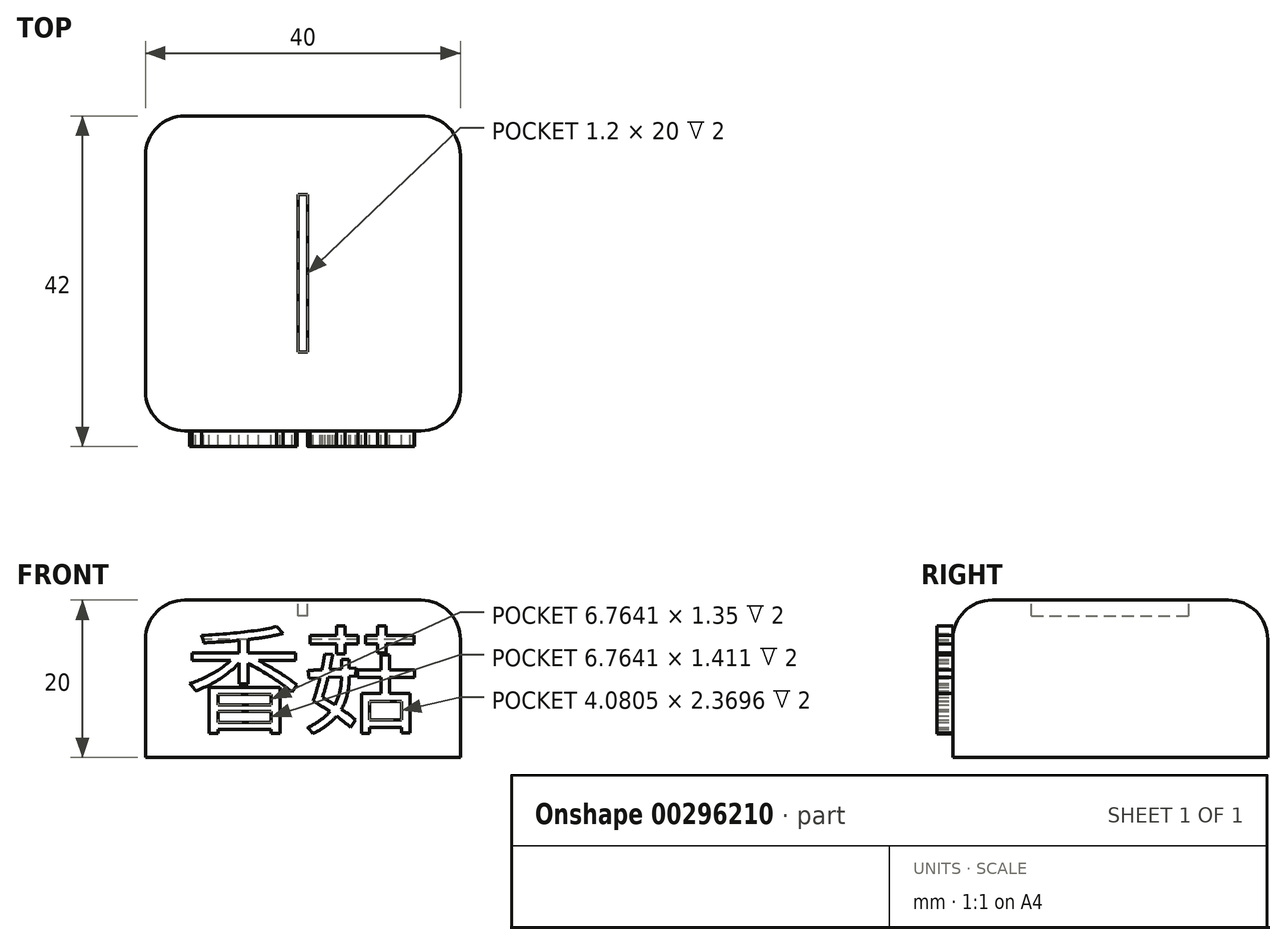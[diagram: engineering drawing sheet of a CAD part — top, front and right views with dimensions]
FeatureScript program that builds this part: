
annotation { "Feature Type Name" : "Feature", "Feature Type Description" : "" }
export const myFeature = defineFeature(function(context is Context, id is Id, definition is map)
    precondition{}
    {
        {
            var Q0;
            Q0=qCreatedBy(makeId("Top.planeOp"),FACE);
            var sketch = newSketch(context, id + "F0", { "sketchPlane" : qUnion([Q0])});
            skLineSegment(sketch, "E0.bottom", {"start": v(20, -20) * mm, "end": v(-20, -20) * mm});
            skLineSegment(sketch, "E0.top", {"start": v(20, 20) * mm, "end": v(-20, 20) * mm});
            skLineSegment(sketch, "E0.left", {"start": v(20, -20) * mm, "end": v(20, 20) * mm});
            skLineSegment(sketch, "E0.right", {"start": v(-20, -20) * mm, "end": v(-20, 20) * mm});
            skPoint(sketch, "E0.middle", {"position": v(0, 0) * mm});
            skLineSegment(sketch, "E1.bottom", {"start": v(0.6, -10) * mm, "end": v(-0.6, -10) * mm});
            skLineSegment(sketch, "E1.top", {"start": v(0.6, 10) * mm, "end": v(-0.6, 10) * mm});
            skLineSegment(sketch, "E1.left", {"start": v(0.6, -10) * mm, "end": v(0.6, 10) * mm});
            skLineSegment(sketch, "E1.right", {"start": v(-0.6, -10) * mm, "end": v(-0.6, 10) * mm});
            skSolve(sketch);
        }
        {
            var Q0;
            Q0=makeQuery(id+"F0.imprint","IMPRINT",FACE,{"disambiguationData":[TD([[makeQuery(id+"F0.imprint","IMPRINT",EDGE,{"derivedFrom":sQuery(id+"F0.wireOp",EDGE,"E0.bottom")}),-1.0]])]});
            var Q1;
            Q1=makeQuery(id+"F0.imprint","IMPRINT",FACE,{"disambiguationData":[TD([[makeQuery(id+"F0.imprint","IMPRINT",EDGE,{"derivedFrom":sQuery(id+"F0.wireOp",EDGE,"E1.bottom")}),-1.0]])]});
            extrude(context, id + "F1", {"entities" : qUnion([Q0, Q1]), "oppositeDirection" : true, "depth" : 20 * mm});
        }
        {
            var Q0;
            Q0=makeQuery(id+"F0.imprint","IMPRINT",FACE,{"disambiguationData":[TD([[makeQuery(id+"F0.imprint","IMPRINT",EDGE,{"derivedFrom":sQuery(id+"F0.wireOp",EDGE,"E1.bottom")}),-1.0]])]});
            extrude(context, id + "F2", {"entities" : qUnion([Q0]), "operationType" : NewBodyOperationType.REMOVE, "oppositeDirection" : true, "depth" : 2 * mm});
        }
        {
            var Q0;
            Q0=makeQuery(id+"F2.boolean.opBoolean","COPY",EDGE,{"derivedFrom":makeQuery(id+"F2.opExtrude","CAP_EDGE",EDGE,{"disambiguationData":[OSD([sQuery(id+"F0.wireOp",EDGE,"E1.left")])],"isStart":true})});
            var Q1;
            Q1=makeQuery(id+"F2.boolean.opBoolean","COPY",EDGE,{"derivedFrom":makeQuery(id+"F2.opExtrude","CAP_EDGE",EDGE,{"disambiguationData":[OSD([sQuery(id+"F0.wireOp",EDGE,"E1.right")])],"isStart":true})});
            var Q2;
            Q2=makeQuery(id+"F1.opExtrude","SWEPT_EDGE",EDGE,{"disambiguationData":[OSD([sQuery(id+"F0.wireOp",EDGE,"E0.bottom"),sQuery(id+"F0.wireOp",EDGE,"E0.left")])]});
            var Q3;
            Q3=makeQuery(id+"F1.opExtrude","SWEPT_EDGE",EDGE,{"disambiguationData":[OSD([sQuery(id+"F0.wireOp",EDGE,"E0.top"),sQuery(id+"F0.wireOp",EDGE,"E0.left")])]});
            var Q4;
            Q4=makeQuery(id+"F1.opExtrude","CAP_EDGE",EDGE,{"disambiguationData":[OSD([sQuery(id+"F0.wireOp",EDGE,"E0.left")])],"isStart":true});
            var Q5;
            Q5=makeQuery(id+"F1.opExtrude","SWEPT_EDGE",EDGE,{"disambiguationData":[OSD([sQuery(id+"F0.wireOp",EDGE,"E0.bottom"),sQuery(id+"F0.wireOp",EDGE,"E0.right")])]});
            var Q6;
            Q6=makeQuery(id+"F1.opExtrude","SWEPT_EDGE",EDGE,{"disambiguationData":[OSD([sQuery(id+"F0.wireOp",EDGE,"E0.top"),sQuery(id+"F0.wireOp",EDGE,"E0.right")])]});
            var Q7;
            Q7=makeQuery(id+"F1.opExtrude","CAP_EDGE",EDGE,{"disambiguationData":[OSD([sQuery(id+"F0.wireOp",EDGE,"E0.top")])],"isStart":true});
            var Q8;
            Q8=makeQuery(id+"F1.opExtrude","CAP_EDGE",EDGE,{"disambiguationData":[OSD([sQuery(id+"F0.wireOp",EDGE,"E0.right")])],"isStart":true});
            var Q9;
            Q9=makeQuery(id+"F1.opExtrude","CAP_EDGE",EDGE,{"disambiguationData":[OSD([sQuery(id+"F0.wireOp",EDGE,"E0.bottom")])],"isStart":true});
            fillet(context, id + "F3", {"entities" : qUnion([Q0, Q1, Q2, Q3, Q4, Q5, Q6, Q7, Q8, Q9]), "radius" : 5 * mm, "tangentPropagation" : true, "allowEdgeOverflow" : false});
        }
        {
            var Q0;
            Q0=makeQuery(id+"F1.opExtrude","SWEPT_FACE",FACE,{"disambiguationData":[OSD([sQuery(id+"F0.wireOp",EDGE,"E0.bottom")])]});
            var sketch = newSketch(context, id + "F4", { "sketchPlane" : qUnion([Q0])});
            skText(sketch, "E2", { "text": "香菇", "fontName": "NotoSansCJKtc-Regular.otf"});
            const initialGuessF4  = {"E2": [-0.015, -0.0158, 1, 0, 0.0108]};
            skSetInitialGuess(sketch, initialGuessF4);
            skSolve(sketch);
        }
        {
            var Q0;
            {var subQ5=sQuery(id+"F4.wireOp",EDGE,"E2.sketch_text.stroke-19");Q0=makeQuery(id+"F4.imprint","IMPRINT",FACE,{"disambiguationData":[TD([[makeQuery(id+"F4.imprint","IMPRINT",EDGE,{"derivedFrom":subQ5}),1.0]])]});}
            var Q1;
            Q1=makeQuery(id+"F4.imprint","IMPRINT",FACE,{"disambiguationData":[TD([[makeQuery(id+"F4.imprint","IMPRINT",EDGE,{"derivedFrom":sQuery(id+"F4.wireOp",EDGE,"E2.sketch_text.stroke-16")}),1.0]])]});
            var Q2;
            Q2=makeQuery(id+"F4.imprint","IMPRINT",FACE,{"disambiguationData":[TD([[makeQuery(id+"F4.imprint","IMPRINT",EDGE,{"derivedFrom":sQuery(id+"F4.wireOp",EDGE,"E2.sketch_text.stroke-0")}),1.0]])]});
            var Q3;
            Q3=makeQuery(id+"F4.imprint","IMPRINT",FACE,{"disambiguationData":[TD([[makeQuery(id+"F4.imprint","IMPRINT",EDGE,{"derivedFrom":sQuery(id+"F4.wireOp",EDGE,"E2.sketch_text.stroke-50")}),1.0]])]});
            var Q4;
            Q4=makeQuery(id+"F4.imprint","IMPRINT",FACE,{"disambiguationData":[TD([[makeQuery(id+"F4.imprint","IMPRINT",EDGE,{"derivedFrom":sQuery(id+"F4.wireOp",EDGE,"E2.sketch_text.stroke-38")}),1.0]])]});
            var Q5;
            {var subQ0=sQuery(id+"F4.wireOp",EDGE,"E2.sketch_text.stroke-42");Q5=makeQuery(id+"F4.imprint","IMPRINT",FACE,{"disambiguationData":[TD([[makeQuery(id+"F4.imprint","IMPRINT",EDGE,{"derivedFrom":subQ0}),1.0]])]});}
            var Q6;
            {var subQ6=sQuery(id+"F4.wireOp",EDGE,"E2.sketch_text.stroke-54");Q6=makeQuery(id+"F4.imprint","IMPRINT",FACE,{"disambiguationData":[TD([[makeQuery(id+"F4.imprint","IMPRINT",EDGE,{"derivedFrom":subQ6}),1.0]])]});}
            var Q7;
            Q7=makeQuery(id+"F4.imprint","IMPRINT",FACE,{"disambiguationData":[TD([[makeQuery(id+"F4.imprint","IMPRINT",EDGE,{"derivedFrom":sQuery(id+"F4.wireOp",EDGE,"E2.sketch_text.stroke-62")}),1.0]])]});
            var Q8;
            Q8=makeQuery(id+"F4.imprint","IMPRINT",FACE,{"disambiguationData":[TD([[makeQuery(id+"F4.imprint","IMPRINT",EDGE,{"derivedFrom":sQuery(id+"F4.wireOp",EDGE,"E2.sketch_text.stroke-88")}),1.0]])]});
            extrude(context, id + "F5", {"entities" : qUnion([Q0, Q1, Q2, Q3, Q4, Q5, Q6, Q7, Q8]), "operationType" : NewBodyOperationType.ADD, "depth" : 2 * mm});
        }
    });
